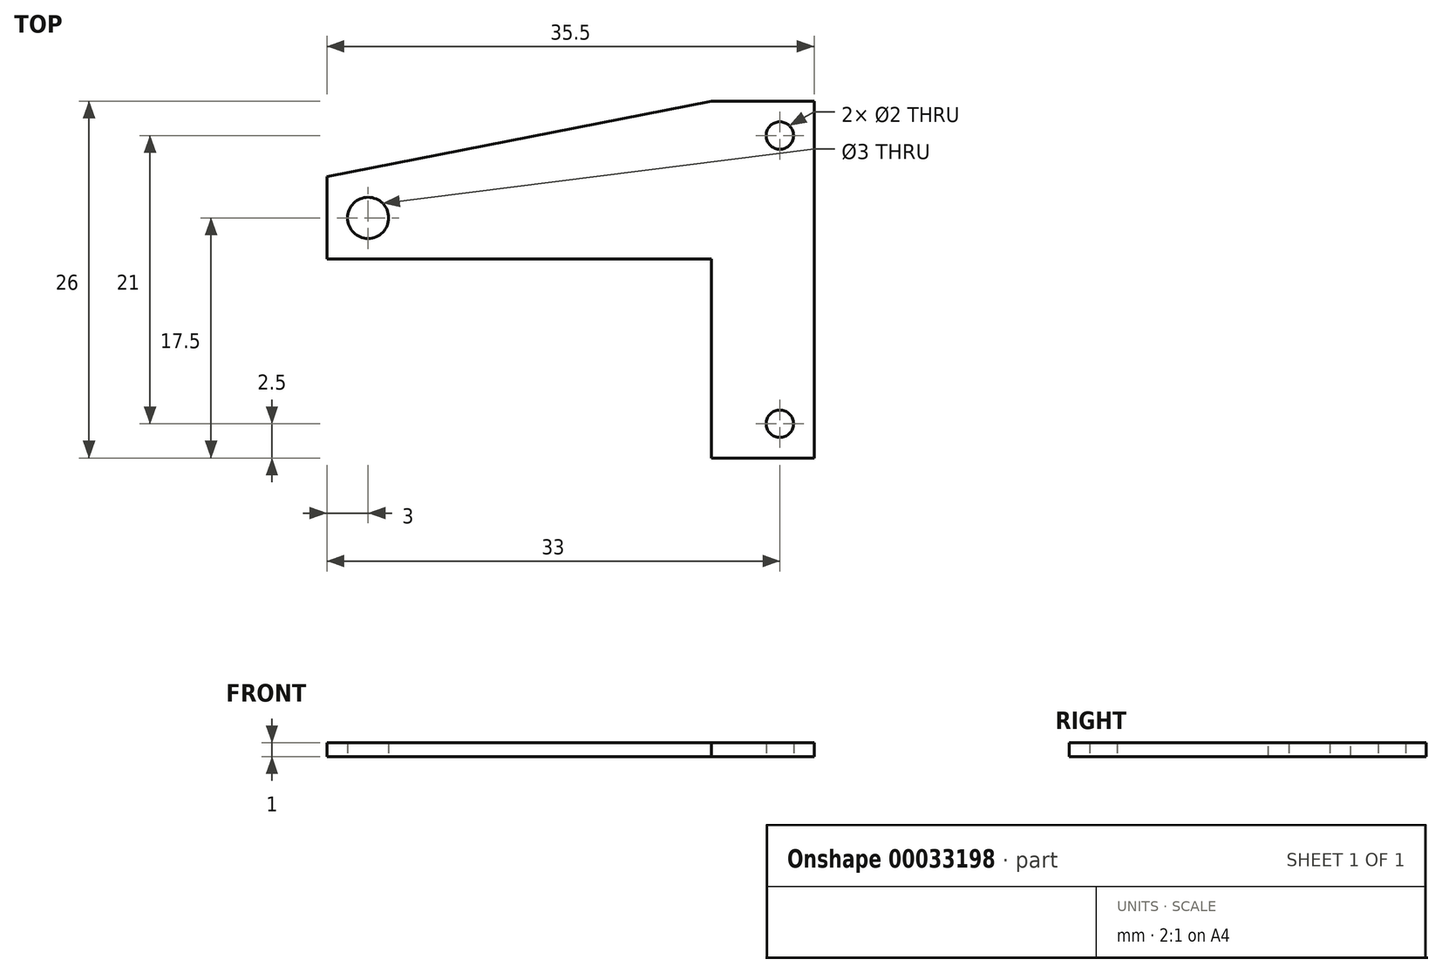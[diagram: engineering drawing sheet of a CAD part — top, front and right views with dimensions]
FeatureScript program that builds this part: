
annotation { "Feature Type Name" : "Feature", "Feature Type Description" : "" }
export const myFeature = defineFeature(function(context is Context, id is Id, definition is map)
    precondition{}
    {
        {
            var Q0;
            Q0=qCreatedBy(makeId("Top.planeOp"),FACE);
            var sketch = newSketch(context, id + "F0", { "sketchPlane" : qUnion([Q0])});
            skLineSegment(sketch, "E0.bottom", {"start": v(-17.75, 13) * mm, "end": v(17.75, 13) * mm});
            skLineSegment(sketch, "E0.top", {"start": v(-17.75, -13) * mm, "end": v(17.75, -13) * mm});
            skLineSegment(sketch, "E0.left", {"start": v(-17.75, 13) * mm, "end": v(-17.75, -13) * mm});
            skLineSegment(sketch, "E0.right", {"start": v(17.75, 13) * mm, "end": v(17.75, -13) * mm});
            skPoint(sketch, "E0.middle", {"position": v(0, 0) * mm});
            skCircle(sketch, "E1", {"center": v(15.25, 10.5) * mm, "radius": 1 * mm});
            skCircle(sketch, "E2", {"center": v(-14.75, 4.5) * mm, "radius": 1.5 * mm});
            skCircle(sketch, "E3.MirrorC", {"center": v(15.25, -10.5) * mm, "radius": 1 * mm});
            skSolve(sketch);
        }
        {
            var Q0;
            Q0 = qSketchRegion(id + "F0", true);
            extrude(context, id + "F1", {"entities" : qUnion([Q0]), "depth" : 1 * mm});
        }
        {
            var Q0;
            Q0=makeQuery(id+"F1.opExtrude","CAP_FACE",FACE,{"disambiguationData":[OSD([sQuery(id+"F0.wireOp",EDGE,"E0.bottom"),sQuery(id+"F0.wireOp",EDGE,"E0.top"),sQuery(id+"F0.wireOp",EDGE,"E0.left"),sQuery(id+"F0.wireOp",EDGE,"E0.right"),sQuery(id+"F0.wireOp",EDGE,"E1"),sQuery(id+"F0.wireOp",EDGE,"E2"),sQuery(id+"F0.wireOp",EDGE,"E3.MirrorC")])],"isStart":false});
            var sketch = newSketch(context, id + "F2", { "sketchPlane" : qUnion([Q0])});
            skLineSegment(sketch, "E4.bottom", {"start": v(-17.75, -13) * mm, "end": v(10.25, -13) * mm});
            skLineSegment(sketch, "E4.top", {"start": v(-17.75, 1.5) * mm, "end": v(10.25, 1.5) * mm});
            skLineSegment(sketch, "E4.left", {"start": v(-17.75, -13) * mm, "end": v(-17.75, 1.5) * mm});
            skLineSegment(sketch, "E4.right", {"start": v(10.25, -13) * mm, "end": v(10.25, 1.5) * mm});
            skLineSegment(sketch, "E5.0.0", {"start": v(-17.75, 13) * mm, "end": v(-17.75, -13) * mm, "construction": true});
            skLineSegment(sketch, "E5.0.1", {"start": v(-17.75, -13) * mm, "end": v(17.75, -13) * mm, "construction": true});
            skLineSegment(sketch, "E5.0.2", {"start": v(17.75, -13) * mm, "end": v(17.75, 13) * mm, "construction": true});
            skLineSegment(sketch, "E5.0.3", {"start": v(17.75, 13) * mm, "end": v(-17.75, 13) * mm, "construction": true});
            skCircle(sketch, "E6.0", {"center": v(-14.75, 4.5) * mm, "radius": 1.5 * mm, "construction": true});
            skCircle(sketch, "E7.0", {"center": v(15.25, 10.5) * mm, "radius": 1 * mm, "construction": true});
            skLineSegment(sketch, "E8", {"start": v(-17.75, 7.5) * mm, "end": v(10.25, 13) * mm});
            skLineSegment(sketch, "E9", {"start": v(10.25, 13) * mm, "end": v(-17.75, 13) * mm});
            skLineSegment(sketch, "E10", {"start": v(-17.75, 7.5) * mm, "end": v(-17.75, 13) * mm});
            skSolve(sketch);
        }
        {
            var Q0;
            Q0 = qSketchRegion(id + "F2", true);
            extrude(context, id + "F3", {"entities" : qUnion([Q0]), "operationType" : NewBodyOperationType.REMOVE, "endBound" : BoundingType.UP_TO_NEXT, "oppositeDirection" : true, "depth" : 25 * mm});
        }
    });
